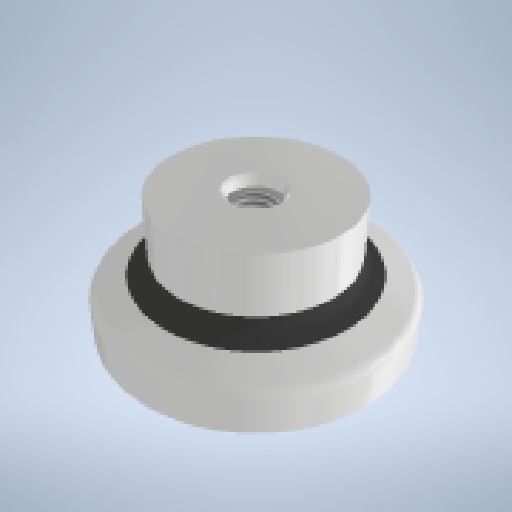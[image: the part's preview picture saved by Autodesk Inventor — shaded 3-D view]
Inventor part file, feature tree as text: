
AUTODESK INVENTOR PART (.ipt)
format: ipt  version: 2024 (Build 280153000, 153)  size: 564,224 bytes
history: native  units: mm
features: sketch x6, other x4, revolve x3, fillet x3, hole x2, chamfer x2, extrude x2, plane x1, projected_geometry x1
ambient origin geometry x8: Origin, YZ Plane, XZ Plane, XY Plane, X Axis, Y Axis, Z Axis, Center Point
bodies: Body1 (feature_tree), Body2 (feature_tree), Body3 (feature_tree), Body4 (feature_tree)
feature tree (24):
  other  "Mount"
  sketch  "Sketch1"  dims[d0=16.0mm d1=10.0mm]
  revolve  "Revolution1"  [1 undecoded]
  revolve  "Revolution2"  [1 undecoded]
  revolve  "Revolution3"  [1 undecoded]
  fillet  "Fillet1"  Radius=4.0mm
  fillet  "Fillet2"  Radius=4.0mm
  hole  "Hole1"  [1 undecoded]
  chamfer  "Chamfer1"  Distance=25.0mm
  plane  "Work Plane1"
  extrude  "Extrusion1"  TaperAngle=360.0deg  [1 undecoded]
  fillet  "Fillet3"  Radius=1.5mm
  sketch  "Sketch4"  dims[d9=5.0mm d10=2.0mm]
  extrude  "Extrusion2"  Depth=1.0mm
  hole  "Hole2"  [1 undecoded]
  chamfer  "Chamfer2"  Distance=1.0mm
  other  "Damper and Pad"
  other  "Cap"
  sketch  "Sketch2"  dims[d2=105.0deg d3=18.0mm]
  sketch  "Sketch3"  dims[d4=9.0mm d5=19.198622mm d6=4.0mm d8=4.0mm]
  sketch  "Sketch5"  dims[d11=2.0mm]
  other  "Leveling Nut"
  sketch  "Sketch6"  dims[d12=0.5mm d13=25.0mm d14=360.0deg d15=1.5mm d16=1.0mm d17=1.5mm d18=1.0mm d19=3.0mm d20=1.5mm d21=4.0mm d22=1.5mm d23=1.5mm d24=1.5mm d25=360.0deg d26=360.0deg d27=2.0mm d28=2.0mm d29=9.0mm d30=16.0mm d31=4.0mm d32=2.0mm d33=90.0deg d34=8.0mm d35=20.594885mm d36=2.0mm d37=2.0mm d38=45.0deg d39=-5.5mm d40=24.0mm d41=8.0mm d42=60.0mm d44=360.0deg d46=6.6mm d47=0.0mm d48=1.0mm d49=0.3mm d50=6.35mm d51=0.0mm d52=6.647mm d53=16.0mm d54=4.0mm d55=2.0mm d56=90.0deg d57=8.0mm d58=20.594885mm d59=0.5mm d60=2.0mm d61=45.0deg]
  projected_geometry  "Project Cut Edges1"
note: 6 required parameter values undecoded (feature->parameter linkage not recoverable at this tier; creation-order binding heuristic only, values carry confidence <= 0.55)